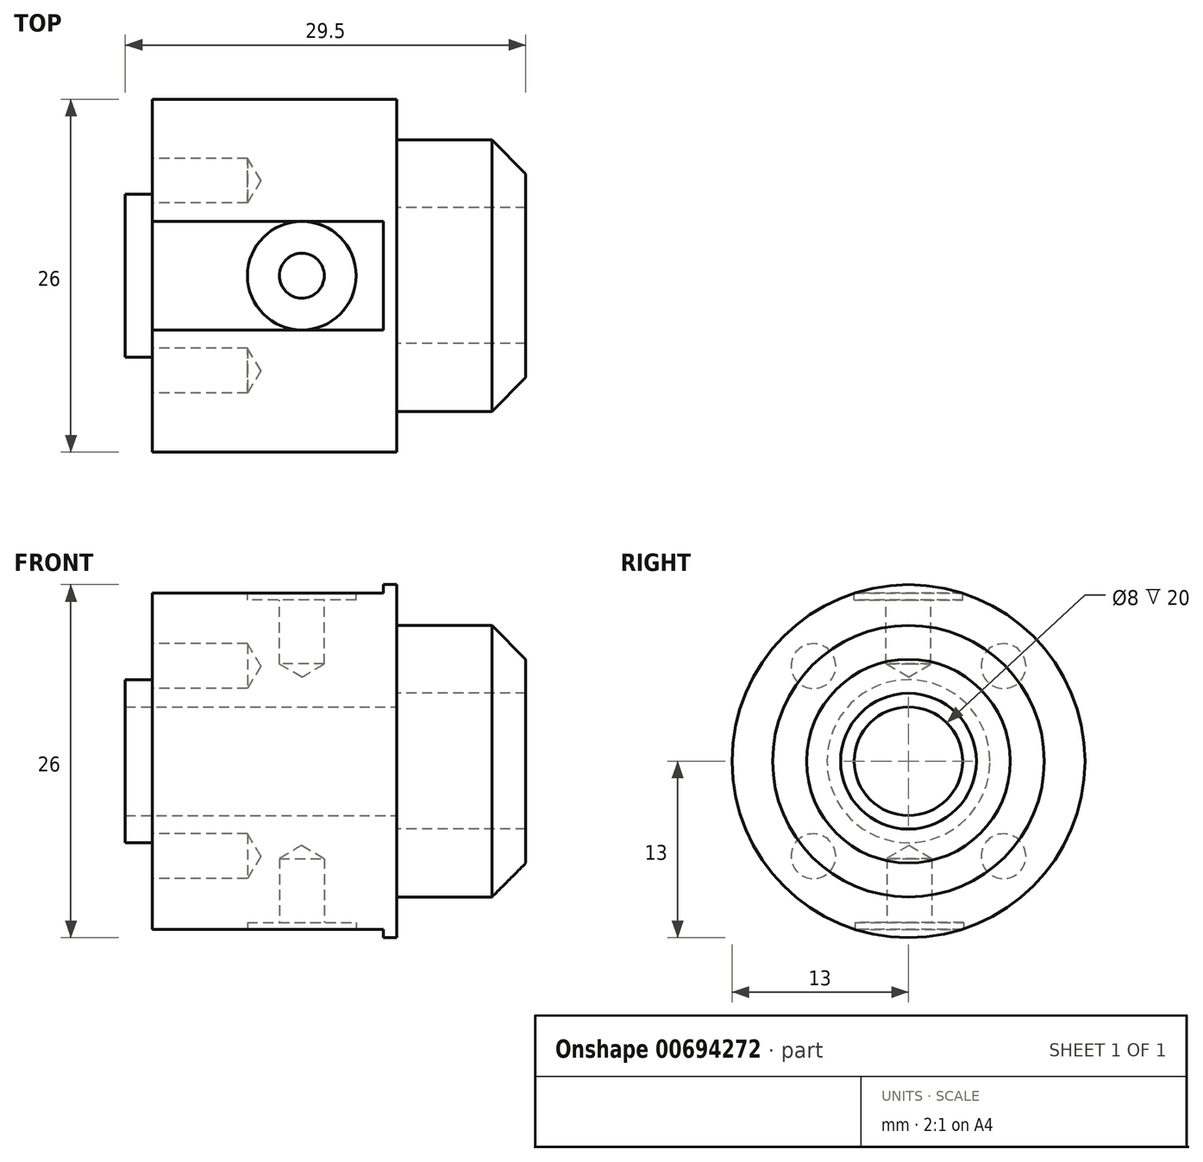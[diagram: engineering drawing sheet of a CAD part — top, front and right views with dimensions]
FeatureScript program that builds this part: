
annotation { "Feature Type Name" : "Feature", "Feature Type Description" : "" }
export const myFeature = defineFeature(function(context is Context, id is Id, definition is map)
    precondition{}
    {
        {
            var Q0;
            Q0=qCreatedBy(makeId("Front.planeOp"),FACE);
            var sketch = newSketch(context, id + "F0", { "sketchPlane" : qUnion([Q0])});
            skLineSegment(sketch, "E0", {"start": v(0, 4) * mm, "end": v(0, 13) * mm});
            skLineSegment(sketch, "E1", {"start": v(0, 13) * mm, "end": v(-18, 13) * mm});
            skLineSegment(sketch, "E2", {"start": v(-18, 13) * mm, "end": v(-18, 6) * mm});
            skLineSegment(sketch, "E3", {"start": v(-18, 6) * mm, "end": v(-20, 6) * mm});
            skLineSegment(sketch, "E4", {"start": v(-20, 6) * mm, "end": v(-20, 4) * mm});
            skPoint(sketch, "E5.startSnap0", {"position": v(0, 6.5) * mm});
            skLineSegment(sketch, "E6", {"start": v(0, 4) * mm, "end": v(-20, 4) * mm});
            skPoint(sketch, "E7.end.orphan", {"position": v(0, 0) * mm});
            skPoint(sketch, "E8.orphan", {"position": v(-20, 0) * mm});
            skLineSegment(sketch, "E9", {"start": v(0, 0) * mm, "end": v(-15.28, 0) * mm, "construction": true});
            skSolve(sketch);
        }
        {
            var Q0;
            Q0=qSketchRegion(id+"F0",true);
            var Q1;
            Q1=sQuery(id+"F0.wireOp",EDGE,"E9");
            revolve(context, id + "F1", {"entities" : qUnion([Q0]), "axis" : qUnion([Q1]), "revolveType" : RevolveType.FULL});
        }
        {
            var Q0;
            Q0=makeQuery(id+"F1.opRevolve","SWEPT_FACE",FACE,{"disambiguationData":[OSD([sQuery(id+"F0.wireOp",EDGE,"E2")])]});
            var sketch = newSketch(context, id + "F2", { "sketchPlane" : qUnion([Q0])});
            skCircle(sketch, "E10", {"center": v(7, 7) * mm, "radius": 1.5 * mm});
            skCircle(sketch, "E11.1.0", {"center": v(-7, 7) * mm, "radius": 1.5 * mm});
            skCircle(sketch, "E11.2.0", {"center": v(-7, -7) * mm, "radius": 1.5 * mm});
            skCircle(sketch, "E11.3.0", {"center": v(7, -7) * mm, "radius": 1.5 * mm});
            skPoint(sketch, "E11.center", {"position": v(0, 0) * mm});
            skSolve(sketch);
        }
        {
            var Q0;
            Q0=sQuery(id+"F2.wireOp",VERTEX,"E11.1.0.center");
            var Q1;
            Q1=sQuery(id+"F2.wireOp",VERTEX,"E10.center");
            var Q2;
            Q2=sQuery(id+"F2.wireOp",VERTEX,"E11.2.0.center");
            var Q3;
            Q3=sQuery(id+"F2.wireOp",VERTEX,"E11.3.0.center");
            var Q4;
            Q4=makeQuery(id+"F1.opRevolve","SWEPT_BODY",BODY,{"disambiguationData":[OSD([sQuery(id+"F0.wireOp",EDGE,"E0"),sQuery(id+"F0.wireOp",EDGE,"E1"),sQuery(id+"F0.wireOp",EDGE,"E2"),sQuery(id+"F0.wireOp",EDGE,"E3"),sQuery(id+"F0.wireOp",EDGE,"E4"),sQuery(id+"F0.wireOp",EDGE,"E6")])]});
            hole(context, id + "F3", {"style" : HoleStyle.SIMPLE, "endStyle" : HoleEndStyle.BLIND, "standardTappedOrClearance" : lookupTablePath({ "standard" : "ISO", "engagement" : "75%", "pitch" : "0.7 mm", "size" : "M4", "type" : "Tapped" }), "standardBlindInLast" : lookupTablePath({ "standard" : "ISO", "engagement" : "75%", "pitch" : "0.7 mm", "size" : "M4", "type" : "Tapped" }), "holeDiameter" : 3.3 * mm, "majorDiameter" : 4 * mm, "showTappedDepth" : true, "holeDepth" : 7 * mm, "isTappedThrough" : true, "tappedDepth" : 7 * mm, "tapClearance" : 0, "locations" : qUnion([Q0, Q1, Q2, Q3]), "scope" : qUnion([Q4])});
        }
        {
            var Q0;
            Q0=makeQuery(id+"F1.opRevolve","SWEPT_FACE",FACE,{"disambiguationData":[OSD([sQuery(id+"F0.wireOp",EDGE,"E0")])]});
            var sketch = newSketch(context, id + "F4", { "sketchPlane" : qUnion([Q0])});
            skCircle(sketch, "E12", {"center": v(0, 0) * mm, "radius": 5 * mm});
            skCircle(sketch, "E13", {"center": v(0, 0) * mm, "radius": 10 * mm});
            skSolve(sketch);
        }
        {
            var Q0;
            Q0=qSketchRegion(id+"F4",true);
            extrude(context, id + "F5", {"entities" : qUnion([Q0]), "operationType" : NewBodyOperationType.ADD, "depth" : 9.5 * mm, "offsetDistance" : 25 * mm});
        }
        {
            var Q0;
            Q0=makeQuery(id+"F5.opExtrude","CAP_EDGE",EDGE,{"disambiguationData":[OSD([sQuery(id+"F4.wireOp",EDGE,"E13")])],"isStart":false});
            chamfer(context, id + "F6", {"entities" : qUnion([Q0]), "width" : 2.5 * mm, "tangentPropagation" : true});
        }
        {
            var Q0;
            Q0=makeQuery(id+"F1.opRevolve","SWEPT_FACE",FACE,{"disambiguationData":[OSD([sQuery(id+"F0.wireOp",EDGE,"E2")])]});
            var sketch = newSketch(context, id + "F7", { "sketchPlane" : qUnion([Q0])});
            skArc(sketch, "E14", {"start": v(4, 12.37) * mm, "mid": v(0, 13) * mm, "end": v(-4, 12.37) * mm});
            skLineSegment(sketch, "E15", {"start": v(-4, 12.37) * mm, "end": v(4, 12.37) * mm});
            skLineSegment(sketch, "E16", {"start": v(-4, -12.37) * mm, "end": v(4, -12.37) * mm});
            skArc(sketch, "E17.trimOffspring", {"start": v(-4, -12.37) * mm, "mid": v(0, -13) * mm, "end": v(4, -12.37) * mm});
            skSolve(sketch);
        }
        {
            var Q0;
            Q0=qSketchRegion(id+"F7",true);
            extrude(context, id + "F8", {"entities" : qUnion([Q0]), "operationType" : NewBodyOperationType.REMOVE, "oppositeDirection" : true, "depth" : 17 * mm, "offsetDistance" : 25 * mm});
        }
        {
            var Q0;
            Q0=makeQuery(id+"F8.boolean.opBoolean","COPY",FACE,{"derivedFrom":makeQuery(id+"F8.opExtrude","SWEPT_FACE",FACE,{"disambiguationData":[OSD([sQuery(id+"F7.wireOp",EDGE,"E15")])]})});
            var sketch = newSketch(context, id + "F9", { "sketchPlane" : qUnion([Q0])});
            skCircle(sketch, "E18", {"center": v(-7, 0) * mm, "radius": 2.97 * mm});
            skSolve(sketch);
        }
        {
            var Q0;
            Q0=sQuery(id+"F9.wireOp",VERTEX,"E18.center");
            var Q1;
            Q1=makeQuery(id+"F1.opRevolve","SWEPT_BODY",BODY,{"disambiguationData":[OSD([sQuery(id+"F0.wireOp",EDGE,"E0"),sQuery(id+"F0.wireOp",EDGE,"E1"),sQuery(id+"F0.wireOp",EDGE,"E2"),sQuery(id+"F0.wireOp",EDGE,"E3"),sQuery(id+"F0.wireOp",EDGE,"E4"),sQuery(id+"F0.wireOp",EDGE,"E6")])]});
            hole(context, id + "F10", {"style" : HoleStyle.SIMPLE, "endStyle" : HoleEndStyle.BLIND, "standardTappedOrClearance" : lookupTablePath({ "standard" : "ISO", "engagement" : "75%", "pitch" : "0.7 mm", "size" : "M4", "type" : "Tapped" }), "standardBlindInLast" : lookupTablePath({ "standard" : "ISO", "engagement" : "75%", "pitch" : "0.7 mm", "size" : "M4", "type" : "Tapped" }), "holeDiameter" : 3.3 * mm, "majorDiameter" : 4 * mm, "showTappedDepth" : true, "holeDepth" : 5.2 * mm, "isTappedThrough" : true, "tappedDepth" : 4.5 * mm, "tapClearance" : 1, "locations" : qUnion([Q0]), "scope" : qUnion([Q1])});
        }
        {
            var Q0;
            Q0=makeQuery(id+"F8.boolean.opBoolean","COPY",FACE,{"derivedFrom":makeQuery(id+"F8.opExtrude","SWEPT_FACE",FACE,{"disambiguationData":[OSD([sQuery(id+"F7.wireOp",EDGE,"E15")])]})});
            var sketch = newSketch(context, id + "F11", { "sketchPlane" : qUnion([Q0])});
            skCircle(sketch, "E19", {"center": v(-7, 0) * mm, "radius": 4 * mm});
            skSolve(sketch);
        }
        {
            var Q0;
            Q0=qSketchRegion(id+"F11",true);
            extrude(context, id + "F12", {"entities" : qUnion([Q0]), "operationType" : NewBodyOperationType.REMOVE, "oppositeDirection" : true, "depth" : 0.5 * mm, "offsetDistance" : 25 * mm});
        }
        {
            var Q0;
            Q0=makeQuery(id+"F8.boolean.opBoolean","COPY",FACE,{"derivedFrom":makeQuery(id+"F8.opExtrude","SWEPT_FACE",FACE,{"disambiguationData":[OSD([sQuery(id+"F7.wireOp",EDGE,"E16")])]})});
            var sketch = newSketch(context, id + "F13", { "sketchPlane" : qUnion([Q0])});
            skCircle(sketch, "E20", {"center": v(-7, -0.05) * mm, "radius": 3.25 * mm});
            skSolve(sketch);
        }
        {
            var Q0;
            Q0=sQuery(id+"F13.wireOp",VERTEX,"E20.center");
            var Q1;
            Q1=makeQuery(id+"F1.opRevolve","SWEPT_BODY",BODY,{"disambiguationData":[OSD([sQuery(id+"F0.wireOp",EDGE,"E0"),sQuery(id+"F0.wireOp",EDGE,"E1"),sQuery(id+"F0.wireOp",EDGE,"E2"),sQuery(id+"F0.wireOp",EDGE,"E3"),sQuery(id+"F0.wireOp",EDGE,"E4"),sQuery(id+"F0.wireOp",EDGE,"E6")])]});
            hole(context, id + "F14", {"style" : HoleStyle.SIMPLE, "endStyle" : HoleEndStyle.BLIND, "standardTappedOrClearance" : lookupTablePath({ "standard" : "ISO", "engagement" : "75%", "pitch" : "0.7 mm", "size" : "M4", "type" : "Tapped" }), "standardBlindInLast" : lookupTablePath({ "standard" : "ISO", "engagement" : "75%", "pitch" : "0.7 mm", "size" : "M4", "type" : "Tapped" }), "holeDiameter" : 3.3 * mm, "majorDiameter" : 4 * mm, "showTappedDepth" : true, "holeDepth" : 5.2 * mm, "isTappedThrough" : true, "tappedDepth" : 4.5 * mm, "tapClearance" : 1, "locations" : qUnion([Q0]), "scope" : qUnion([Q1])});
        }
        {
            var Q0;
            Q0=makeQuery(id+"F8.boolean.opBoolean","COPY",FACE,{"derivedFrom":makeQuery(id+"F8.opExtrude","SWEPT_FACE",FACE,{"disambiguationData":[OSD([sQuery(id+"F7.wireOp",EDGE,"E16")])]})});
            var sketch = newSketch(context, id + "F15", { "sketchPlane" : qUnion([Q0])});
            skCircle(sketch, "E21", {"center": v(-7, -0.05) * mm, "radius": 4 * mm});
            skSolve(sketch);
        }
        {
            var Q0;
            Q0=qSketchRegion(id+"F15",true);
            extrude(context, id + "F16", {"entities" : qUnion([Q0]), "operationType" : NewBodyOperationType.REMOVE, "oppositeDirection" : true, "depth" : 0.5 * mm, "offsetDistance" : 25 * mm});
        }
    });
